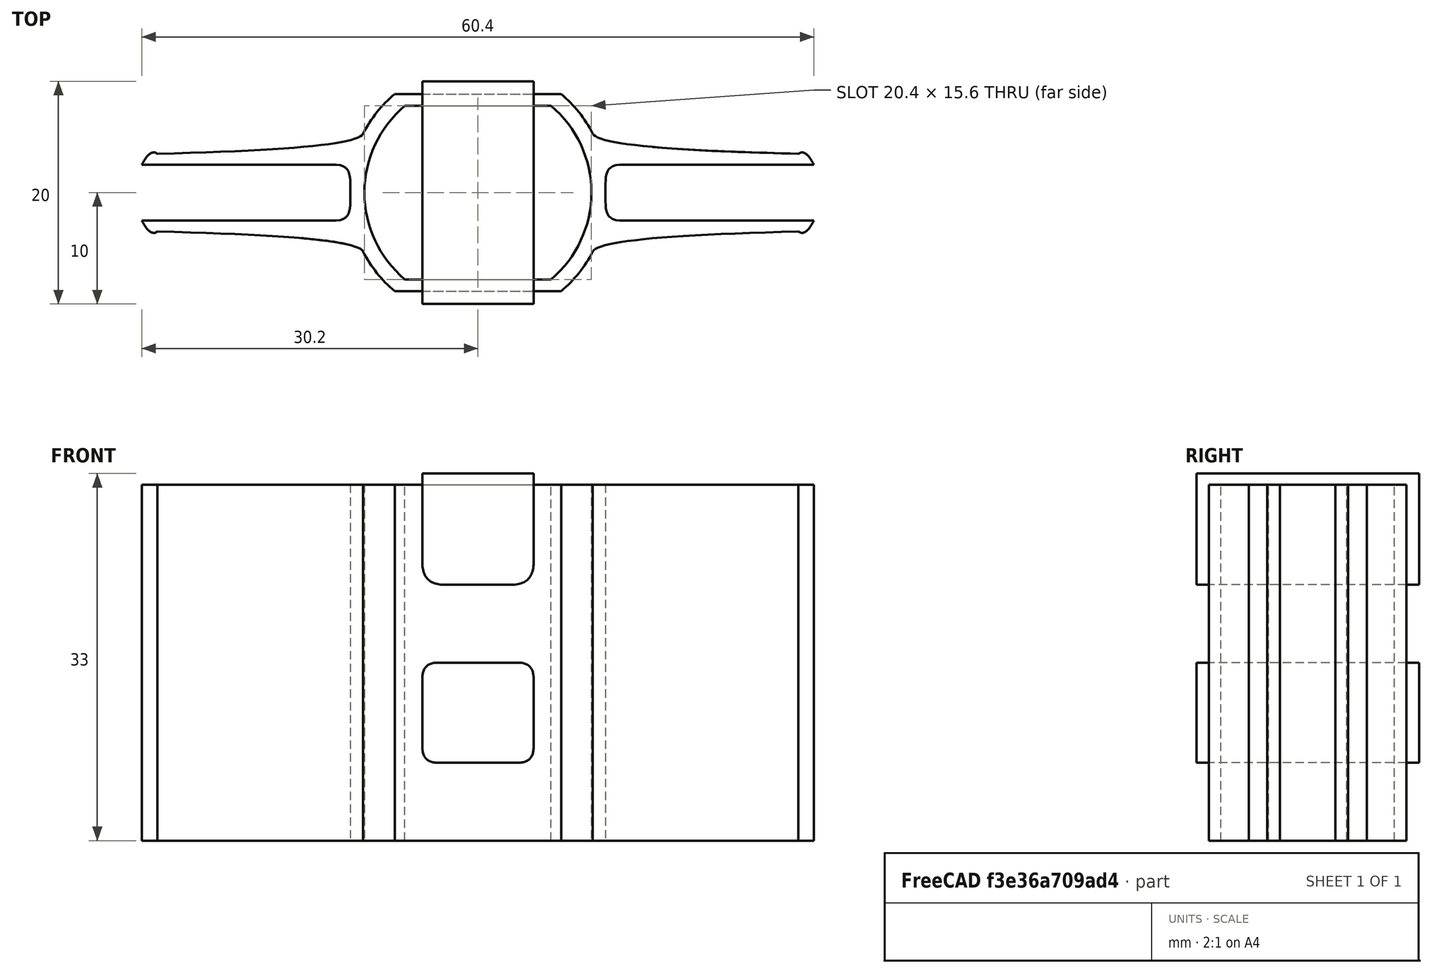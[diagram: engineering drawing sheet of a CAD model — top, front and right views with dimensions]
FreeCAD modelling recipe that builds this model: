
FCSTD DOCUMENT  (FreeCAD 0.19R0.19.2)
Label: 019
License: All rights reserved
LicenseURL: http://en.wikipedia.org/wiki/All_rights_reserved
objects: Sketcher::SketchObject×2, Part::Extrusion×2
note: 4 computed .brp shape members not serialized (recipe doc carries the construction recipe); baked Part::Feature solids carry a one-line shape summary decoded from their .brp

FEATURE [Sketcher::SketchObject] Sketch  label="main001"
  FullyConstrained = true
  sketch-geometry (80):
    g0: ArcOfCircle CenterX=-3.45031e-07 CenterY=0 CenterZ=0 NormalX=0 NormalY=0 NormalZ=1 AngleXU=0 Radius=10.2 StartAngle=5.4126 EndAngle=7.15377
    g1: ArcOfCircle CenterX=-3.45031e-07 CenterY=0 CenterZ=0 NormalX=0 NormalY=0 NormalZ=1 AngleXU=0 Radius=10.2 StartAngle=2.27101 EndAngle=4.01218
    g2: LineSegment StartX=-6.57267 StartY=7.8 StartZ=0 EndX=6.57267 EndY=7.8 EndZ=0
    g3: LineSegment StartX=-6.57267 StartY=-7.8 StartZ=0 EndX=6.57267 EndY=-7.8 EndZ=0
    g4: ArcOfCircle CenterX=-3.45031e-07 CenterY=0 CenterZ=0 NormalX=0 NormalY=0 NormalZ=1 AngleXU=0 Radius=11.6 StartAngle=2.27101 EndAngle=2.66709
    g5: ArcOfCircle CenterX=-3.45031e-07 CenterY=0 CenterZ=0 NormalX=0 NormalY=0 NormalZ=1 AngleXU=0 Radius=11.6 StartAngle=5.4126 EndAngle=5.80868
    g6: LineSegment StartX=-7.4748 StartY=8.87059 StartZ=0 EndX=7.4748 EndY=8.87059 EndZ=0
    g7: LineSegment StartX=-7.4748 StartY=-8.87059 StartZ=0 EndX=7.4748 EndY=-8.87059 EndZ=0
    g8: ArcOfCircle CenterX=-3.45031e-07 CenterY=0 CenterZ=0 NormalX=0 NormalY=0 NormalZ=1 AngleXU=0 Radius=11.6 StartAngle=3.6161 EndAngle=4.01218
    g9: ArcOfCircle CenterX=-3.45031e-07 CenterY=0 CenterZ=0 NormalX=0 NormalY=0 NormalZ=1 AngleXU=0 Radius=11.6 StartAngle=0.474503 EndAngle=0.870585
    g10: Circle CenterX=-28.8 CenterY=3.5 CenterZ=0 NormalX=0 NormalY=0 NormalZ=1 AngleXU=0 Radius=1
    g11: Circle CenterX=-10.9247 CenterY=3.9 CenterZ=0 NormalX=0 NormalY=0 NormalZ=1 AngleXU=0 Radius=1
    g12: Circle CenterX=-10.3184 CenterY=5.3 CenterZ=0 NormalX=0 NormalY=0 NormalZ=1 AngleXU=0 Radius=1
    g13: BSplineCurve PolesCount=3 KnotsCount=2 Degree=2 IsPeriodic=0
    g14: GeomPoint X=-28.8 Y=3.5 Z=0
    g15: GeomPoint X=-10.3184 Y=5.3 Z=0
    g16: Circle CenterX=28.8 CenterY=3.5 CenterZ=0 NormalX=0 NormalY=0 NormalZ=1 AngleXU=0 Radius=1
    g17: Circle CenterX=10.9247 CenterY=3.9 CenterZ=0 NormalX=0 NormalY=0 NormalZ=1 AngleXU=0 Radius=1
    g18: Circle CenterX=10.3184 CenterY=5.3 CenterZ=0 NormalX=0 NormalY=0 NormalZ=1 AngleXU=0 Radius=1
    g19: BSplineCurve PolesCount=3 KnotsCount=2 Degree=2 IsPeriodic=0
    g20: GeomPoint X=28.8 Y=3.5 Z=0
    g21: GeomPoint X=10.3184 Y=5.3 Z=0
    g22: Circle CenterX=-28.8 CenterY=-3.5 CenterZ=0 NormalX=0 NormalY=0 NormalZ=1 AngleXU=0 Radius=1
    g23: Circle CenterX=-10.9247 CenterY=-3.9 CenterZ=0 NormalX=0 NormalY=0 NormalZ=1 AngleXU=0 Radius=1
    g24: Circle CenterX=-10.3184 CenterY=-5.3 CenterZ=0 NormalX=0 NormalY=0 NormalZ=1 AngleXU=0 Radius=1
    g25: BSplineCurve PolesCount=3 KnotsCount=2 Degree=2 IsPeriodic=0
    g26: GeomPoint X=-28.8 Y=-3.5 Z=0
    g27: GeomPoint X=-10.3184 Y=-5.3 Z=0
    g28: Circle CenterX=28.8 CenterY=-3.5 CenterZ=0 NormalX=0 NormalY=0 NormalZ=1 AngleXU=0 Radius=1
    g29: Circle CenterX=10.9247 CenterY=-3.9 CenterZ=0 NormalX=0 NormalY=0 NormalZ=1 AngleXU=0 Radius=1
    g30: Circle CenterX=10.3184 CenterY=-5.3 CenterZ=0 NormalX=0 NormalY=0 NormalZ=1 AngleXU=0 Radius=1
    g31: BSplineCurve PolesCount=3 KnotsCount=2 Degree=2 IsPeriodic=0
    g32: GeomPoint X=28.8 Y=-3.5 Z=0
    g33: GeomPoint X=10.3184 Y=-5.3 Z=0
    g34-g38: Circle x5 (B-spline internal-alignment scaffolding for g39; pole/knot coordinates omitted)
    g39: BSplineCurve PolesCount=5 KnotsCount=3 Degree=3 IsPeriodic=0
    g40: GeomPoint X=12.7274 Y=2.5 Z=0
    g41: GeomPoint X=11.4637 Y=2.49999e-07 Z=0
    g42: GeomPoint X=12.7274 Y=-2.5 Z=0
    g43-g47: Circle x5 (B-spline internal-alignment scaffolding for g48; pole/knot coordinates omitted)
    g48: BSplineCurve PolesCount=5 KnotsCount=3 Degree=3 IsPeriodic=0
    g49: GeomPoint X=-12.7274 Y=2.5 Z=0
    g50: GeomPoint X=-11.4637 Y=2.50004e-07 Z=0
    g51: GeomPoint X=-12.7274 Y=-2.5 Z=0
    g52: LineSegment StartX=-30.2 StartY=-2.5 StartZ=0 EndX=-12.7274 EndY=-2.5 EndZ=0
    g53: LineSegment StartX=-30.2 StartY=2.5 StartZ=0 EndX=-12.7274 EndY=2.5 EndZ=0
    g54: LineSegment StartX=30.2 StartY=2.5 StartZ=0 EndX=12.7274 EndY=2.5 EndZ=0
    g55: LineSegment StartX=30.2 StartY=-2.5 StartZ=0 EndX=12.7274 EndY=-2.5 EndZ=0
    g56: Circle CenterX=-30.2 CenterY=2.5 CenterZ=0 NormalX=0 NormalY=0 NormalZ=1 AngleXU=0 Radius=1
    g57: Circle CenterX=-29.4304 CenterY=3.99253 CenterZ=0 NormalX=0 NormalY=0 NormalZ=1 AngleXU=0 Radius=1
    g58: Circle CenterX=-28.8 CenterY=3.5 CenterZ=0 NormalX=0 NormalY=0 NormalZ=1 AngleXU=0 Radius=1
    g59: BSplineCurve PolesCount=3 KnotsCount=2 Degree=2 IsPeriodic=0
    g60: GeomPoint X=-30.2 Y=2.5 Z=0
    g61: GeomPoint X=-28.8 Y=3.5 Z=0
    g62: Circle CenterX=30.2 CenterY=-2.5 CenterZ=0 NormalX=0 NormalY=0 NormalZ=1 AngleXU=0 Radius=1
    g63: Circle CenterX=29.4304 CenterY=-3.99253 CenterZ=0 NormalX=0 NormalY=0 NormalZ=1 AngleXU=0 Radius=1
    g64: Circle CenterX=28.8 CenterY=-3.5 CenterZ=0 NormalX=0 NormalY=0 NormalZ=1 AngleXU=0 Radius=1
    g65: BSplineCurve PolesCount=3 KnotsCount=2 Degree=2 IsPeriodic=0
    g66: GeomPoint X=30.2 Y=-2.5 Z=0
    g67: GeomPoint X=28.8 Y=-3.5 Z=0
    g68: Circle CenterX=30.2 CenterY=2.5 CenterZ=0 NormalX=0 NormalY=0 NormalZ=1 AngleXU=0 Radius=1
    g69: Circle CenterX=29.4304 CenterY=3.99253 CenterZ=0 NormalX=0 NormalY=0 NormalZ=1 AngleXU=0 Radius=1
    g70: Circle CenterX=28.8 CenterY=3.5 CenterZ=0 NormalX=0 NormalY=0 NormalZ=1 AngleXU=0 Radius=1
    g71: BSplineCurve PolesCount=3 KnotsCount=2 Degree=2 IsPeriodic=0
    g72: GeomPoint X=30.2 Y=2.5 Z=0
    g73: GeomPoint X=28.8 Y=3.5 Z=0
    g74: Circle CenterX=-30.2 CenterY=-2.5 CenterZ=0 NormalX=0 NormalY=0 NormalZ=1 AngleXU=0 Radius=1
    g75: Circle CenterX=-29.4304 CenterY=-3.99253 CenterZ=0 NormalX=0 NormalY=0 NormalZ=1 AngleXU=0 Radius=1
    g76: Circle CenterX=-28.8 CenterY=-3.5 CenterZ=0 NormalX=0 NormalY=0 NormalZ=1 AngleXU=0 Radius=1
    g77: BSplineCurve PolesCount=3 KnotsCount=2 Degree=2 IsPeriodic=0
    g78: GeomPoint X=-30.2 Y=-2.5 Z=0
    g79: GeomPoint X=-28.8 Y=-3.5 Z=0
  constraints (131):
    c: Block(g0)
    c: Equal(g0,g1)
    c: Coincident(g0,g1)
    c: Coincident(g2,g1)
    c: Coincident(g2,g0)
    c: Horizontal(g2)
    c: Coincident(g3,g1)
    c: Coincident(g3,g0)
    c: Horizontal(g3)
    c: Block(g2)
    c: Block(g3)
    c: Coincident(g4,g0)
    c: Coincident(g5,g0)
    c: Block(g5)
    c: Block(g4)
    c: Coincident(g6,g4)
    c: Coincident(g6,g9)
    c: Horizontal(g6)
    c: Coincident(g7,g8)
    c: Coincident(g7,g5)
    c: Horizontal(g7)
    c: Equal(g4,g8)
    c: Coincident(g4,g8)
    c: Equal(g5,g9)
    c: Coincident(g5,g9)
    c: Block(g8)
    c: Block(g9)
    c: Weight(g10) = 1
    c: Equal(g10,g11)
    c: Equal(g10,g12)
    c: Coincident(g13,g4)
    c: InternalAlignment(g10,g13)
    c: InternalAlignment(g11,g13)
    c: InternalAlignment(g12,g13)
    c: InternalAlignment(g14,g13)
    c: InternalAlignment(g15,g13)
    c: Weight(g16) = 1
    c: Equal(g16,g17)
    c: Equal(g16,g18)
    c: Coincident(g19,g9)
    c: InternalAlignment(g16,g19)
    c: InternalAlignment(g17,g19)
    c: InternalAlignment(g18,g19)
    c: InternalAlignment(g20,g19)
    c: InternalAlignment(g21,g19)
    c: Weight(g22) = 1
    c: Equal(g22,g23)
    c: Equal(g22,g24)
    c: Coincident(g25,g8)
    c: InternalAlignment(g22,g25)
    c: InternalAlignment(g23,g25)
    c: InternalAlignment(g24,g25)
    c: InternalAlignment(g26,g25)
    c: InternalAlignment(g27,g25)
    c: Weight(g28) = 1
    c: Equal(g28,g29)
    c: Equal(g28,g30)
    c: Coincident(g31,g5)
    c: InternalAlignment(g28,g31)
    c: InternalAlignment(g29,g31)
    c: InternalAlignment(g30,g31)
    c: InternalAlignment(g32,g31)
    c: InternalAlignment(g33,g31)
    c: Block(g19)
    c: Block(g13)
    c: Block(g31)
    c: Block(g25)
    c: Weight(g34) = 1
    c: Equal(g34, g35-g38) x4
    c: InternalAlignment(g34-g38 -> g39) x5
    c: InternalAlignment(g40,g39)
    c: InternalAlignment(g41,g39)
    c: InternalAlignment(g42,g39)
    c: Weight(g43) = 1
    c: Equal(g43,g44)
    c: Equal(g43,g45)
    c: Equal(g43,g46)
    c: InternalAlignment(g43-g47 -> g48) x5
    c: InternalAlignment(g49,g48)
    c: InternalAlignment(g50,g48)
    c: InternalAlignment(g51,g48)
    c: Block(g48)
    c: Block(g39)
    c: Coincident(g52,g48)
    c: Tangent(g52,g22)
    c: Coincident(g53,g48)
    c: Tangent(g53,g10)
    c: Coincident(g54,g39)
    c: Tangent(g54,g16)
    c: Coincident(g55,g39)
    c: Tangent(g55,g28)
    c: Weight(g56) = 1
    c: Equal(g56,g57)
    c: Equal(g56,g58)
    c: InternalAlignment(g56,g59)
    c: InternalAlignment(g57,g59)
    c: InternalAlignment(g58,g59)
    c: InternalAlignment(g60,g59)
    c: InternalAlignment(g61,g59)
    c: Weight(g62) = 1
    c: Equal(g62,g63)
    c: Equal(g62,g64)
    c: InternalAlignment(g62,g65)
    c: InternalAlignment(g63,g65)
    c: InternalAlignment(g64,g65)
    c: InternalAlignment(g66,g65)
    c: InternalAlignment(g67,g65)
    c: Weight(g68) = 1
    c: Equal(g68,g69)
    c: Equal(g68,g70)
    c: InternalAlignment(g68,g71)
    c: InternalAlignment(g69,g71)
    c: InternalAlignment(g70,g71)
    c: InternalAlignment(g72,g71)
    c: InternalAlignment(g73,g71)
    c: Block(g71)
    c: Block(g54)
    c: Block(g65)
    c: Block(g55)
    c: Weight(g74) = 1
    c: Equal(g74,g75)
    c: Equal(g74,g76)
    c: InternalAlignment(g74,g77)
    c: InternalAlignment(g75,g77)
    c: InternalAlignment(g76,g77)
    c: InternalAlignment(g78,g77)
    c: InternalAlignment(g79,g77)
    c: Block(g77)
    c: Block(g52)
    c: Block(g59)
    c: Block(g53)
FEATURE [Part::Extrusion] Extrude  label="main"
  Base = -> Sketch
  Dir = (0,0,1)
  DirMode = 2
  FaceMakerClass = Part::FaceMakerBullseye
  LengthFwd = 32
  LengthRev = 0
  Solid = true
  Symmetric = false
FEATURE [Sketcher::SketchObject] Sketch001  label="mainCollingAndStructuralHoles"
  FullyConstrained = true
  Placement = pos=(0,0,0) rot=(-1,0,0;4.71239rad)
  sketch-geometry (44):
    g0: Circle CenterX=-5 CenterY=2 CenterZ=0 NormalX=0 NormalY=0 NormalZ=1 AngleXU=0 Radius=1
    g1: Circle CenterX=-5 CenterY=0 CenterZ=0 NormalX=0 NormalY=0 NormalZ=1 AngleXU=0 Radius=1
    g2: Circle CenterX=-3 CenterY=4.6505e-12 CenterZ=0 NormalX=0 NormalY=0 NormalZ=1 AngleXU=0 Radius=1
    g3: BSplineCurve PolesCount=3 KnotsCount=2 Degree=2 IsPeriodic=0
    g4: GeomPoint X=-5 Y=2 Z=0
    g5: GeomPoint X=-3 Y=4.6505e-12 Z=0
    g6: Circle CenterX=5 CenterY=2 CenterZ=0 NormalX=0 NormalY=0 NormalZ=1 AngleXU=0 Radius=1
    g7: Circle CenterX=5 CenterY=4.6505e-12 CenterZ=0 NormalX=0 NormalY=0 NormalZ=1 AngleXU=0 Radius=1
    g8: Circle CenterX=3 CenterY=4.6505e-12 CenterZ=0 NormalX=0 NormalY=0 NormalZ=1 AngleXU=0 Radius=1
    g9: BSplineCurve PolesCount=3 KnotsCount=2 Degree=2 IsPeriodic=0
    g10: GeomPoint X=5 Y=2 Z=0
    g11: GeomPoint X=3 Y=4.6505e-12 Z=0
    g12: LineSegment StartX=5 StartY=2 StartZ=0 EndX=5 EndY=10 EndZ=0
    g13: LineSegment StartX=-5 StartY=2 StartZ=0 EndX=-5 EndY=10 EndZ=0
    g14: LineSegment StartX=-3 StartY=4.6505e-12 StartZ=0 EndX=3 EndY=4.6505e-12 EndZ=0
    g15: LineSegment StartX=-5 StartY=10 StartZ=0 EndX=5 EndY=10 EndZ=0
    g16: Circle CenterX=-3.6 CenterY=-7 CenterZ=0 NormalX=0 NormalY=0 NormalZ=1 AngleXU=0 Radius=1
    g17: Circle CenterX=-5 CenterY=-7 CenterZ=0 NormalX=0 NormalY=0 NormalZ=1 AngleXU=0 Radius=1
    g18: Circle CenterX=-5 CenterY=-8.4 CenterZ=0 NormalX=0 NormalY=0 NormalZ=1 AngleXU=0 Radius=1
    g19: BSplineCurve PolesCount=3 KnotsCount=2 Degree=2 IsPeriodic=0
    g20: GeomPoint X=-3.6 Y=-7 Z=0
    g21: GeomPoint X=-5 Y=-8.4 Z=0
    g22: Circle CenterX=5 CenterY=-8.4 CenterZ=0 NormalX=0 NormalY=0 NormalZ=1 AngleXU=0 Radius=1
    g23: Circle CenterX=5 CenterY=-7 CenterZ=0 NormalX=0 NormalY=0 NormalZ=1 AngleXU=0 Radius=1
    g24: Circle CenterX=3.6 CenterY=-7 CenterZ=0 NormalX=0 NormalY=0 NormalZ=1 AngleXU=0 Radius=1
    g25: BSplineCurve PolesCount=3 KnotsCount=2 Degree=2 IsPeriodic=0
    g26: GeomPoint X=5 Y=-8.4 Z=0
    g27: GeomPoint X=3.6 Y=-7 Z=0
    g28: Circle CenterX=-3.6 CenterY=-16 CenterZ=0 NormalX=0 NormalY=0 NormalZ=1 AngleXU=0 Radius=1
    g29: Circle CenterX=-5 CenterY=-16 CenterZ=0 NormalX=0 NormalY=0 NormalZ=1 AngleXU=0 Radius=1
    g30: Circle CenterX=-5 CenterY=-14.6 CenterZ=0 NormalX=0 NormalY=0 NormalZ=1 AngleXU=0 Radius=1
    g31: BSplineCurve PolesCount=3 KnotsCount=2 Degree=2 IsPeriodic=0
    g32: GeomPoint X=-3.6 Y=-16 Z=0
    g33: GeomPoint X=-5 Y=-14.6 Z=0
    g34: Circle CenterX=5 CenterY=-14.6 CenterZ=0 NormalX=0 NormalY=0 NormalZ=1 AngleXU=0 Radius=1
    g35: Circle CenterX=5 CenterY=-16 CenterZ=0 NormalX=0 NormalY=0 NormalZ=1 AngleXU=0 Radius=1
    g36: Circle CenterX=3.6 CenterY=-16 CenterZ=0 NormalX=0 NormalY=0 NormalZ=1 AngleXU=0 Radius=1
    g37: BSplineCurve PolesCount=3 KnotsCount=2 Degree=2 IsPeriodic=0
    g38: GeomPoint X=5 Y=-14.6 Z=0
    g39: GeomPoint X=3.6 Y=-16 Z=0
    g40: LineSegment StartX=-3.6 StartY=-7 StartZ=0 EndX=3.6 EndY=-7 EndZ=0
    g41: LineSegment StartX=-5 StartY=-8.4 StartZ=0 EndX=-5 EndY=-14.6 EndZ=0
    g42: LineSegment StartX=-3.6 StartY=-16 StartZ=0 EndX=3.6 EndY=-16 EndZ=0
    g43: LineSegment StartX=5 StartY=-14.6 StartZ=0 EndX=5 EndY=-8.4 EndZ=0
  constraints (79):
    c: Weight(g0) = 1
    c: Equal(g0,g1)
    c: Equal(g0,g2)
    c: InternalAlignment(g0,g3)
    c: InternalAlignment(g1,g3)
    c: InternalAlignment(g2,g3)
    c: InternalAlignment(g4,g3)
    c: InternalAlignment(g5,g3)
    c: Weight(g6) = 1
    c: Equal(g6,g7)
    c: Equal(g6,g8)
    c: InternalAlignment(g6,g9)
    c: InternalAlignment(g7,g9)
    c: InternalAlignment(g8,g9)
    c: InternalAlignment(g10,g9)
    c: InternalAlignment(g11,g9)
    c: Block(g3)
    c: Coincident(g13,g3)
    c: Block(g9)
    c: Coincident(g12,g9)
    c: Vertical(g12)
    c: Block(g12)
    c: Block(g13)
    c: Coincident(g14,g3)
    c: Coincident(g14,g9)
    c: Horizontal(g14)
    c: Coincident(g15,g13)
    c: Coincident(g15,g12)
    c: Horizontal(g15)
    c: Distance(g12) = 8
    c: Distance(g15) = 10
    c: Weight(g16) = 1
    c: Equal(g16,g17)
    c: Equal(g16,g18)
    c: InternalAlignment(g16,g19)
    c: InternalAlignment(g17,g19)
    c: InternalAlignment(g18,g19)
    c: InternalAlignment(g20,g19)
    c: InternalAlignment(g21,g19)
    c: Weight(g22) = 1
    c: Equal(g22,g23)
    c: Equal(g22,g24)
    c: InternalAlignment(g22,g25)
    c: InternalAlignment(g23,g25)
    c: InternalAlignment(g24,g25)
    c: InternalAlignment(g26,g25)
    c: InternalAlignment(g27,g25)
    c: Weight(g28) = 1
    c: Equal(g28,g29)
    c: Equal(g28,g30)
    c: InternalAlignment(g28,g31)
    c: InternalAlignment(g29,g31)
    c: InternalAlignment(g30,g31)
    c: InternalAlignment(g32,g31)
    c: InternalAlignment(g33,g31)
    c: Weight(g34) = 1
    c: Equal(g34,g35)
    c: Equal(g34,g36)
    c: InternalAlignment(g34,g37)
    c: InternalAlignment(g35,g37)
    c: InternalAlignment(g36,g37)
    c: InternalAlignment(g38,g37)
    c: InternalAlignment(g39,g37)
    c: Block(g25)
    c: Block(g37)
    c: Block(g31)
    c: Block(g19)
    c: Coincident(g40,g19)
    c: Coincident(g40,g25)
    c: Horizontal(g40)
    c: Coincident(g41,g19)
    c: Coincident(g41,g31)
    c: Vertical(g41)
    c: Coincident(g42,g31)
    c: Coincident(g42,g37)
    c: Horizontal(g42)
    c: Coincident(g43,g37)
    c: Coincident(g43,g25)
    c: Vertical(g43)
FEATURE [Part::Extrusion] Extrude001  label="mainCollingAndStructuralHoles001"
  Base = -> Sketch001
  Dir = (0,-1,3e-16)
  DirMode = 2
  FaceMakerClass = Part::FaceMakerBullseye
  LengthFwd = 20
  LengthRev = 0
  Placement = pos=(0,10,23) rot=(0,0,1;0rad)
  Solid = true
  Symmetric = false
